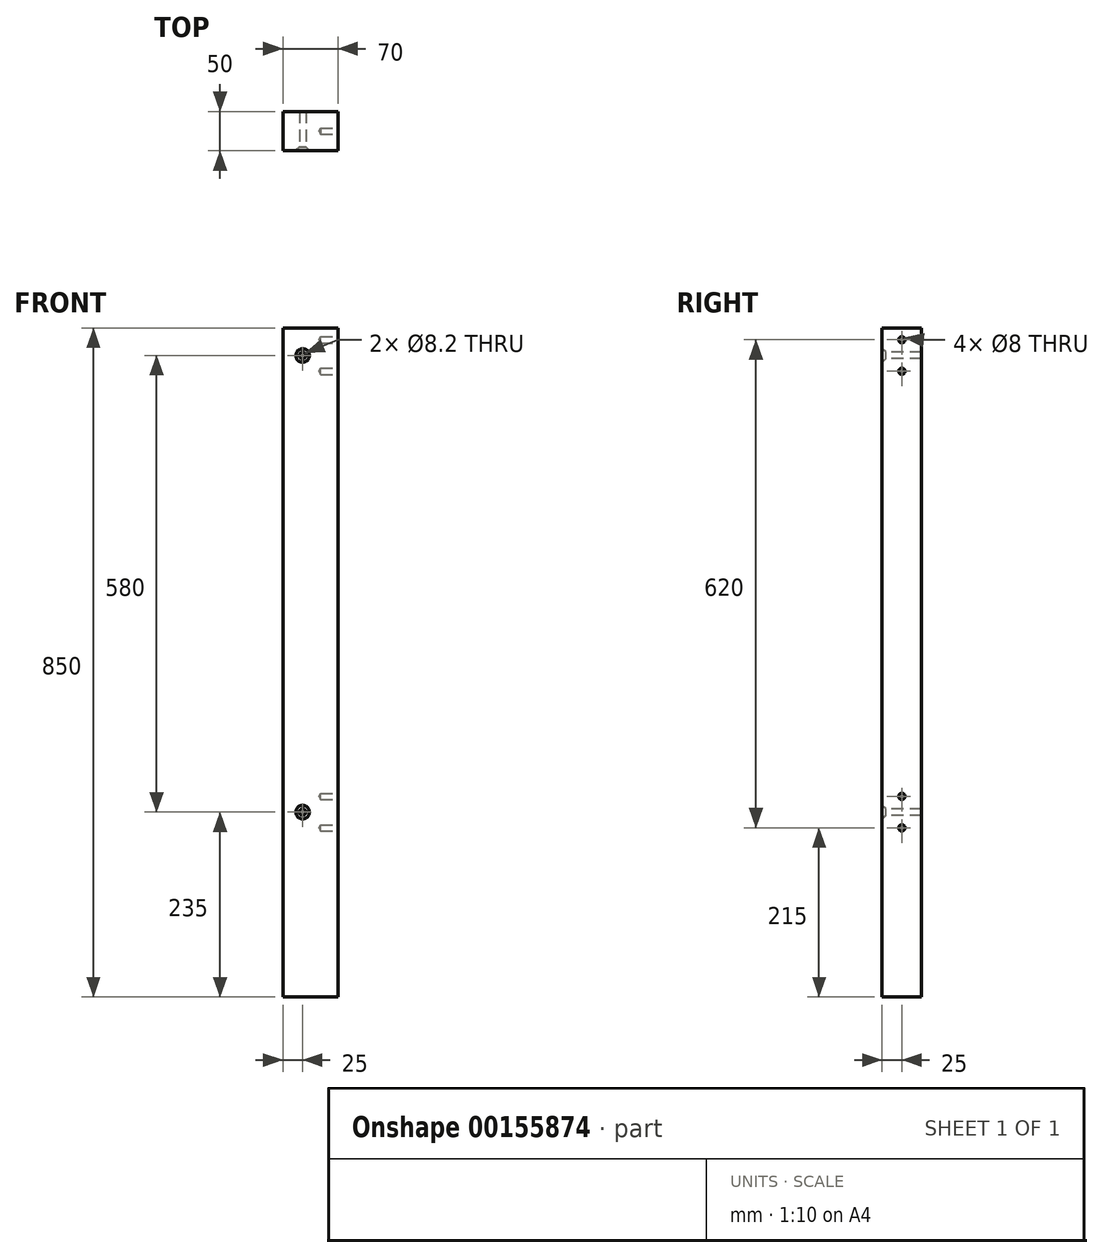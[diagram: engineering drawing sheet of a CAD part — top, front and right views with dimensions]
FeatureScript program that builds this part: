
annotation { "Feature Type Name" : "Feature", "Feature Type Description" : "" }
export const myFeature = defineFeature(function(context is Context, id is Id, definition is map)
    precondition{}
    {
        {
            var Q0;
            Q0=qCreatedBy(makeId("Top.planeOp"),FACE);
            var sketch = newSketch(context, id + "F0", { "sketchPlane" : qUnion([Q0])});
            skLineSegment(sketch, "E0.bottom", {"start": v(35, 25) * mm, "end": v(-35, 25) * mm});
            skLineSegment(sketch, "E0.top", {"start": v(35, -25) * mm, "end": v(-35, -25) * mm});
            skLineSegment(sketch, "E0.left", {"start": v(35, 25) * mm, "end": v(35, -25) * mm});
            skLineSegment(sketch, "E0.right", {"start": v(-35, 25) * mm, "end": v(-35, -25) * mm});
            skPoint(sketch, "E0.middle", {"position": v(0, 0) * mm});
            skSolve(sketch);
        }
        {
            var Q0;
            Q0=makeQuery(id+"F0.imprint","IMPRINT",FACE,{"disambiguationData":[TD([[makeQuery(id+"F0.imprint","IMPRINT",EDGE,{"derivedFrom":sQuery(id+"F0.wireOp",EDGE,"E0.bottom")}),1.0]])]});
            extrude(context, id + "F1", {"entities" : qUnion([Q0]), "depth" : 850 * mm});
        }
        {
            var Q0;
            Q0=makeQuery(id+"F1.opExtrude","SWEPT_FACE",FACE,{"disambiguationData":[OSD([sQuery(id+"F0.wireOp",EDGE,"E0.left")])]});
            var sketch = newSketch(context, id + "F2", { "sketchPlane" : qUnion([Q0])});
            skPoint(sketch, "E1", {"position": v(0, 215) * mm});
            skPoint(sketch, "E2", {"position": v(0, 255) * mm});
            skPoint(sketch, "E3", {"position": v(0, 795) * mm});
            skPoint(sketch, "E4", {"position": v(0, 835) * mm});
            skSolve(sketch);
        }
        {
            var Q0;
            Q0=sQuery(id+"F2.wireOp",VERTEX,"E1");
            var Q1;
            Q1=sQuery(id+"F2.wireOp",VERTEX,"E2");
            var Q2;
            Q2=sQuery(id+"F2.wireOp",VERTEX,"E3");
            var Q3;
            Q3=sQuery(id+"F2.wireOp",VERTEX,"E4");
            var Q4;
            Q4=makeQuery(id+"F1.opExtrude","SWEPT_BODY",BODY,{"disambiguationData":[OSD([sQuery(id+"F0.wireOp",EDGE,"E0.bottom"),sQuery(id+"F0.wireOp",EDGE,"E0.top"),sQuery(id+"F0.wireOp",EDGE,"E0.left"),sQuery(id+"F0.wireOp",EDGE,"E0.right")])]});
            hole(context, id + "F3", {"style" : HoleStyle.SIMPLE, "endStyle" : HoleEndStyle.BLIND, "holeDiameter" : 8 * mm, "holeDepth" : 22 * mm, "locations" : qUnion([Q0, Q1, Q2, Q3]), "scope" : qUnion([Q4])});
        }
        {
            var Q0;
            Q0=makeQuery(id+"F1.opExtrude","SWEPT_FACE",FACE,{"disambiguationData":[OSD([sQuery(id+"F0.wireOp",EDGE,"E0.top")])]});
            var sketch = newSketch(context, id + "F4", { "sketchPlane" : qUnion([Q0])});
            skPoint(sketch, "E5", {"position": v(-10, 235) * mm});
            skPoint(sketch, "E6", {"position": v(-10, 815) * mm});
            skSolve(sketch);
        }
        {
            var Q0;
            Q0=sQuery(id+"F4.wireOp",VERTEX,"E5");
            var Q1;
            Q1=sQuery(id+"F4.wireOp",VERTEX,"E6");
            var Q2;
            Q2=makeQuery(id+"F1.opExtrude","SWEPT_BODY",BODY,{"disambiguationData":[OSD([sQuery(id+"F0.wireOp",EDGE,"E0.bottom"),sQuery(id+"F0.wireOp",EDGE,"E0.top"),sQuery(id+"F0.wireOp",EDGE,"E0.left"),sQuery(id+"F0.wireOp",EDGE,"E0.right")])]});
            hole(context, id + "F5", {"style" : HoleStyle.C_SINK, "endStyle" : HoleEndStyle.THROUGH, "holeDiameter" : 8.2 * mm, "cSinkDiameter" : 17.3 * mm, "cSinkAngle" : 90 * degree, "locations" : qUnion([Q0, Q1]), "scope" : qUnion([Q2]), "isTappedThrough" : true});
        }
    });
